# Revit family: КА РАШВОРК  арт.500_501
name_source: partatom
category: Арматура трубопроводов
units: mm (PartAtom-declared; Revit-internal decimal feet)

## family parameters
Всегда вертикально = Нет
На основе рабочей плоскости = Нет
Общий = Нет
При загрузке вырезать с полостями = Да
Размер круглого соединителя = Использовать диаметр
Тип детали = Вставляется

## types (37) — shared parameters
ADSK_Единица измерения = шт
ADSK_Завод-изготовитель = ООО "ТД "РАШВОРК"
URL = https://rwru.ru
Изготовитель = ООО "ТД "РАШВОРК"
Корпус = EPDM
Уго_длинна = 115 мм
Фланец = Оц. углеродистая сталь
zero-valued in all types: Отметка по умолчанию

## per-type parameters (varying)
| type | ADSK_Код изделия | ADSK_Масса | D | DN | DN_соединителя | D_2 рез. | Dрез. | L | LL | T | l1 | Контрольные стержни | Смещение | Стержни | Точки |
| Компенсатор антивибрационный РАШВОРК 500-0032-10, DN032, PN10, корпус - EPDM+Nylon, фланец - оцинкованная угл.сталь, Ф/Ф | 500-032-10-EPDM-FF | 2.9 | 70 мм | 32 мм | 32 мм | 38 мм | 75 мм | 95 мм | 48 мм | 15 мм | 1 мм | Контрольные стержни : Котрольные стержни DN700 | 4 мм | Нет | 26 мм |
| Компенсатор антивибрационный РАШВОРК 500-1200-10, DN 1200, PN10, корпус - EPDM+Nylon, фланец - оцинкованная угл.сталь, Ф/Ф В КОМПЛЕКТЕ С КОНТРОЛЬНЫМИ СТЕРЖНЯМИ | 500-1200-10-EPDM-FF | 340 | 728 мм | 1200 мм | 1200 мм | 645 мм | 200 мм | 260 мм | 150 мм | 36 мм | 3 мм | Контрольные стержни : Котрольные стержни DN1200 | 552 мм | Да | 625 мм |
| Компенсатор антивибрационный РАШВОРК 500-0450-10, DN450, PN10, корпус - EPDM+Nylon, фланец - оцинкованная угл.сталь, Ф/Ф | 500-450-10-EPDM-FF | 56.5 | 308 мм | 450 мм | 450 мм | 270 мм | 300 мм | 265 мм | 176 мм | 25 мм | 3 мм | Контрольные стержни : Котрольные стержни DN700 | 115 мм | Нет | 247 мм |
| Компенсатор антивибрационный РАШВОРК 500-0040-10, DN040, PN10, корпус - EPDM+Nylon, фланец - оцинкованная угл.сталь, Ф/Ф | 500-040-10-EPDM-FF | 3.6 | 75 мм | 40 мм | 40 мм | 41 мм | 75 мм | 95 мм | 45 мм | 15 мм | 3 мм | Контрольные стержни : Котрольные стержни DN700 | 4 мм | Нет | 34 мм |
| Компенсатор антивибрационный РАШВОРК 500-0050-10, DN050, PN10, корпус - EPDM+Nylon, фланец - оцинкованная угл.сталь, Ф/Ф | 500-050-10-EPDM-FF | 4.1 | 83 мм | 50 мм | 50 мм | 41 мм | 80 мм | 105 мм | 55 мм | 15 мм | 3 мм | Контрольные стержни : Котрольные стержни DN700 | 5 мм | Нет | 32 мм |
| Компенсатор антивибрационный РАШВОРК 500-0065-10, DN065, PN10, корпус - EPDM+Nylon, фланец - оцинкованная угл.сталь, Ф/Ф | 500-065-10-EPDM-FF | 5.3 | 93 мм | 65 мм | 65 мм | 52 мм | 86 мм | 115 мм | 55 мм | 15 мм | 3 мм | Контрольные стержни : Котрольные стержни DN700 | 7 мм | Нет | 37 мм |
| Компенсатор антивибрационный РАШВОРК 500-0080-10, DN080, PN10, корпус - EPDM+Nylon, фланец - оцинкованная угл.сталь, Ф/Ф | 500-080-10-EPDM-FF | 6.3 | 100 мм | 80 мм | 80 мм | 62 мм | 118 мм | 135 мм | 70 мм | 15 мм | 3 мм | Контрольные стержни : Котрольные стержни DN700 | 2 мм | Нет | 50 мм |
| Компенсатор антивибрационный РАШВОРК 500-0100-10, DN100, PN10, корпус - EPDM+Nylon, фланец - оцинкованная угл.сталь, Ф/Ф | 500-100-10-EPDM-FF | 7.3 | 110 мм | 100 мм | 100 мм | 72 мм | 134 мм | 135 мм | 70 мм | 17 мм | 3 мм | Контрольные стержни : Котрольные стержни DN700 | 2 мм | Нет | 60 мм |
| Компенсатор антивибрационный РАШВОРК 500-0125-10, DN125, PN10, корпус - EPDM+Nylon, фланец - оцинкованная угл.сталь, Ф/Ф | 500-125-10-EPDM-FF | 9.1 | 125 мм | 115 мм | 125 мм | 89 мм | 150 мм | 165 мм | 99 мм | 19 мм | 3 мм | Контрольные стержни : Котрольные стержни DN700 | 1 мм | Нет | 60 мм |
| Компенсатор антивибрационный РАШВОРК 500-0150-10, DN150, PN10, корпус - EPDM+Nylon, фланец - оцинкованная угл.сталь, Ф/Ф | 500-150-10-EPDM-FF | 13.2 | 143 мм | 142 мм | 150 мм | 101 мм | 187 мм | 180 мм | 106 мм | 21 мм | 3 мм | Контрольные стержни : Котрольные стержни DN700 | 1 мм | Нет | 82 мм |
| Компенсатор антивибрационный РАШВОРК 500-0200-10, DN200, PN10, корпус - EPDM+Nylon, фланец - оцинкованная угл.сталь, Ф/Ф | 500-200-10-EPDM-FF | 17.5 | 170 мм | 195 мм | 200 мм | 132 мм | 190 мм | 205 мм | 137 мм | 21 мм | 3 мм | Контрольные стержни : Котрольные стержни DN700 | 26 мм | Нет | 110 мм |
| Компенсатор антивибрационный РАШВОРК 500-0250-10, DN250, PN10, корпус - EPDM+Nylon, фланец - оцинкованная угл.сталь, Ф/Ф | 500-250-10-EPDM-FF | 22.5 | 198 мм | 240 мм | 250 мм | 158 мм | 215 мм | 240 мм | 164 мм | 23 мм | 3 мм | Контрольные стержни : Котрольные стержни DN700 | 45 мм | Нет | 135 мм |
| Компенсатор антивибрационный РАШВОРК 500-0300-10, DN300, PN10, корпус - EPDM+Nylon, фланец - оцинкованная угл.сталь, Ф/Ф | 500-300-10-EPDM-FF | 29.1 | 223 мм | 280 мм | 300 мм | 185 мм | 275 мм | 260 мм | 180 мм | 23 мм | 3 мм | Контрольные стержни : Котрольные стержни DN700 | 42 мм | Нет | 162 мм |
| Компенсатор антивибрационный РАШВОРК 500-0350-10, DN350, PN10, корпус - EPDM+Nylon, фланец - оцинкованная угл.сталь, Ф/Ф | 500-350-10-EPDM-FF | 40.3 | 253 мм | 350 мм | 350 мм | 213 мм | 235 мм | 265 мм | 185 мм | 25 мм | 3 мм | Контрольные стержни : Котрольные стержни DN700 | 90 мм | Нет | 191 мм |
| Компенсатор антивибрационный РАШВОРК 500-0400-10, DN400, PN10, корпус - EPDM+Nylon, фланец - оцинкованная угл.сталь, Ф/Ф | 500-400-10-EPDM-FF | 44.2 | 283 мм | 360 мм | 400 мм | 240 мм | 155 мм | 265 мм | 178 мм | 25 мм | 3 мм | Контрольные стержни : Котрольные стержни DN700 | 160 мм | Нет | 213 мм |
| Компенсатор антивибрационный РАШВОРК 500-0500-10, DN500, PN10, корпус - EPDM+Nylon, фланец - оцинкованная угл.сталь, Ф/Ф | 500-500-10-EPDM-FF | 61.3 | 335 мм | 486 мм | 500 мм | 286 мм | 225 мм | 265 мм | 175 мм | 27 мм | 3 мм | Контрольные стержни : Котрольные стержни DN700 | 173 мм | Нет | 265 мм |
| Компенсатор антивибрационный РАШВОРК 500-0600-10, DN600, PN10, корпус - EPDM+Nylon, фланец - оцинкованная угл.сталь, Ф/Ф | 500-600-10-EPDM-FF | 67.6 | 390 мм | 580 мм | 600 мм | 335 мм | 200 мм | 265 мм | 165 мм | 27 мм | 3 мм | Контрольные стержни : Котрольные стержни DN700 | 243 мм | Нет | 315 мм |
| Компенсатор антивибрационный РАШВОРК 500-0700-10, DN 700, PN10, корпус - EPDM+Nylon, фланец - оцинкованная угл.сталь, Ф/Ф В КОМПЛЕКТЕ С КОНТРОЛЬНЫМИ СТЕРЖНЯМИ | 500-700-10-EPDM-FF | 136 | 448 мм | 700 мм | 700 мм | 395 мм | 200 мм | 260 мм | 156 мм | 32 мм | 3 мм | Контрольные стержни : Котрольные стержни DN700 | 300 мм | Да | 375 мм |
| Компенсатор антивибрационный РАШВОРК 500-0800-10, DN 800, PN10, корпус - EPDM+Nylon, фланец - оцинкованная угл.сталь, Ф/Ф В КОМПЛЕКТЕ С КОНТРОЛЬНЫМИ СТЕРЖНЯМИ | 500-800-10-EPDM-FF | 183 | 508 мм | 800 мм | 800 мм | 445 мм | 200 мм | 260 мм | 156 мм | 34 мм | 3 мм | Контрольные стержни : Котрольные стержни DN800 | 352 мм | Да | 425 мм |
| Компенсатор антивибрационный РАШВОРК 500-0900-10, DN 900, PN10, корпус - EPDM+Nylon, фланец - оцинкованная угл.сталь, Ф/Ф В КОМПЛЕКТЕ С КОНТРОЛЬНЫМИ СТЕРЖНЯМИ | 500-900-10-EPDM-FF | 217 | 558 мм | 900 мм | 900 мм | 495 мм | 200 мм | 260 мм | 150 мм | 36 мм | 3 мм | Контрольные стержни : Котрольные стержни DN900 | 400 мм | Да | 475 мм |
| Компенсатор антивибрационный РАШВОРК 500-1000-10, DN 1000, PN10, корпус - EPDM+Nylon, фланец - оцинкованная угл.сталь, Ф/Ф В КОМПЛЕКТЕ С КОНТРОЛЬНЫМИ СТЕРЖНЯМИ | 500-1000-10-EPDM-FF | 286 | 615 мм | 1000 мм | 1000 мм | 545 мм | 200 мм | 260 мм | 150 мм | 36 мм | 3 мм | Контрольные стержни : Котрольные стержни DN1000 | 450 мм | Да | 525 мм |
| Компенсатор антивибрационный РАШВОРК 501-032-16, DN032, PN16, корпус - EPDM+Nylon, фланец - оцинкованная угл.сталь, Ф/Ф | 501-032-16-EPDM-FF | 2.9 | 70 мм | 32 мм | 32 мм | 38 мм | 75 мм | 95 мм | 48 мм | 15 мм | 1 мм | Контрольные стержни : Котрольные стержни DN700 | 4 мм | Нет | 26 мм |
| Компенсатор антивибрационный РАШВОРК 501-040-16, DN040, PN16, корпус - EPDM+Nylon, фланец - оцинкованная угл.сталь, Ф/Ф | 501-040-16-EPDM-FF | 3.6 | 75 мм | 40 мм | 40 мм | 41 мм | 75 мм | 95 мм | 45 мм | 15 мм | 3 мм | Контрольные стержни : Котрольные стержни DN700 | 4 мм | Нет | 34 мм |
| Компенсатор антивибрационный РАШВОРК 501-050-16, DN050, PN16, корпус - EPDM+Nylon, фланец - оцинкованная угл.сталь, Ф/Ф | 501-050-16-EPDM-FF | 4.1 | 83 мм | 50 мм | 50 мм | 41 мм | 80 мм | 105 мм | 55 мм | 15 мм | 3 мм | Контрольные стержни : Котрольные стержни DN700 | 5 мм | Нет | 32 мм |
| Компенсатор антивибрационный РАШВОРК 501-065-16, DN065, PN16, корпус - EPDM+Nylon, фланец - оцинкованная угл.сталь, Ф/Ф | 501-065-16-EPDM-FF | 5.3 | 93 мм | 65 мм | 65 мм | 52 мм | 86 мм | 115 мм | 55 мм | 15 мм | 3 мм | Контрольные стержни : Котрольные стержни DN700 | 7 мм | Нет | 37 мм |
| Компенсатор антивибрационный РАШВОРК 501-080-16, DN080, PN16, корпус - EPDM+Nylon, фланец - оцинкованная угл.сталь, Ф/Ф | 501-080-16-EPDM-FF | 6.3 | 100 мм | 80 мм | 80 мм | 62 мм | 118 мм | 135 мм | 70 мм | 15 мм | 3 мм | Контрольные стержни : Котрольные стержни DN700 | 2 мм | Нет | 50 мм |
| Компенсатор антивибрационный РАШВОРК 501-100-16, DN100, PN16, корпус - EPDM+Nylon, фланец - оцинкованная угл.сталь, Ф/Ф | 501-100-16-EPDM-FF | 7.3 | 110 мм | 100 мм | 100 мм | 72 мм | 134 мм | 135 мм | 70 мм | 17 мм | 3 мм | Контрольные стержни : Котрольные стержни DN700 | 2 мм | Нет | 60 мм |
| Компенсатор антивибрационный РАШВОРК 501-125-16, DN125, PN16, корпус - EPDM+Nylon, фланец - оцинкованная угл.сталь, Ф/Ф | 501-125-16-EPDM-FF | 9.1 | 125 мм | 115 мм | 125 мм | 89 мм | 150 мм | 165 мм | 99 мм | 19 мм | 3 мм | Контрольные стержни : Котрольные стержни DN700 | 1 мм | Нет | 60 мм |
| Компенсатор антивибрационный РАШВОРК 501-150-16, DN150, PN16, корпус - EPDM+Nylon, фланец - оцинкованная угл.сталь, Ф/Ф | 501-150-16-EPDM-FF | 13.2 | 143 мм | 142 мм | 150 мм | 101 мм | 187 мм | 180 мм | 106 мм | 21 мм | 3 мм | Контрольные стержни : Котрольные стержни DN700 | 1 мм | Нет | 82 мм |
| Компенсатор антивибрационный РАШВОРК 501-200-16, DN200, PN16, корпус - EPDM+Nylon, фланец - оцинкованная угл.сталь, Ф/Ф | 501-200-16-EPDM-FF | 19.7 | 170 мм | 195 мм | 200 мм | 132 мм | 190 мм | 205 мм | 137 мм | 21 мм | 3 мм | Контрольные стержни : Котрольные стержни DN700 | 26 мм | Нет | 110 мм |
| Компенсатор антивибрационный РАШВОРК 501-250-16, DN250, PN16, корпус - EPDM+Nylon, фланец - оцинкованная угл.сталь, Ф/Ф | 501-250-16-EPDM-FF | 25 | 203 мм | 240 мм | 250 мм | 158 мм | 215 мм | 240 мм | 164 мм | 23 мм | 3 мм | Контрольные стержни : Котрольные стержни DN700 | 45 мм | Нет | 135 мм |
| Компенсатор антивибрационный РАШВОРК 501-300-16, DN300, PN16, корпус - EPDM+Nylon, фланец - оцинкованная угл.сталь, Ф/Ф | 501-300-16-EPDM-FF | 30.8 | 230 мм | 280 мм | 300 мм | 185 мм | 275 мм | 260 мм | 180 мм | 25 мм | 3 мм | Контрольные стержни : Котрольные стержни DN700 | 42 мм | Нет | 162 мм |
| Компенсатор антивибрационный РАШВОРК 501-350-16, DN350, PN16, корпус - EPDM+Nylon, фланец - оцинкованная угл.сталь, Ф/Ф | 501-350-16-EPDM-FF | 41.6 | 260 мм | 350 мм | 350 мм | 213 мм | 235 мм | 265 мм | 185 мм | 25 мм | 3 мм | Контрольные стержни : Котрольные стержни DN700 | 90 мм | Нет | 191 мм |
| Компенсатор антивибрационный РАШВОРК 501-400-16, DN400, PN16, корпус - EPDM+Nylon, фланец - оцинкованная угл.сталь, Ф/Ф | 501-400-16-EPDM-FF | 46.5 | 290 мм | 360 мм | 400 мм | 240 мм | 155 мм | 265 мм | 178 мм | 27 мм | 3 мм | Контрольные стержни : Котрольные стержни DN700 | 160 мм | Нет | 213 мм |
| Компенсатор антивибрационный РАШВОРК 501-450-16, DN450, PN16, корпус - EPDM+Nylon, фланец - оцинкованная угл.сталь, Ф/Ф | 501-450-16-EPDM-FF | 58.8 | 320 мм | 450 мм | 450 мм | 270 мм | 300 мм | 265 мм | 176 мм | 29 мм | 3 мм | Контрольные стержни : Котрольные стержни DN700 | 115 мм | Нет | 247 мм |
| Компенсатор антивибрационный РАШВОРК 501-500-16, DN500, PN16, корпус - EPDM+Nylon, фланец - оцинкованная угл.сталь, Ф/Ф | 501-500-16-EPDM-FF | 62.3 | 358 мм | 486 мм | 500 мм | 286 мм | 225 мм | 265 мм | 175 мм | 29 мм | 3 мм | Контрольные стержни : Котрольные стержни DN700 | 173 мм | Нет | 265 мм |
| Компенсатор антивибрационный РАШВОРК 501-600-16, DN600, PN16, корпус - EPDM+Nylon, фланец - оцинкованная угл.сталь, Ф/Ф | 501-600-16-EPDM-FF | 73.1 | 420 мм | 580 мм | 600 мм | 335 мм | 200 мм | 265 мм | 165 мм | 29 мм | 3 мм | Контрольные стержни : Котрольные стержни DN700 | 243 мм | Нет | 315 мм |

note: column(s) folded — value = type name in every type: ADSK_Наименование
